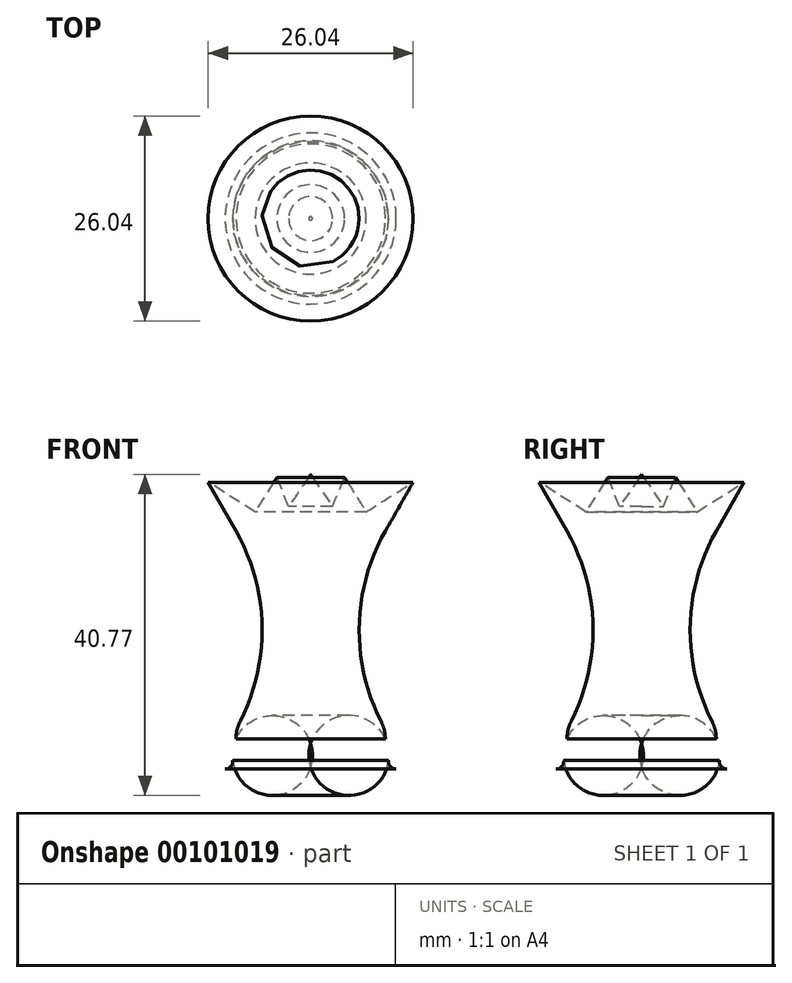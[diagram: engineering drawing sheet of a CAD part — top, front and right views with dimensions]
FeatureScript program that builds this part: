
annotation { "Feature Type Name" : "Feature", "Feature Type Description" : "" }
export const myFeature = defineFeature(function(context is Context, id is Id, definition is map)
    precondition{}
    {
        {
            var Q0;
            Q0=qCreatedBy(makeId("Front.planeOp"),FACE);
            var sketch = newSketch(context, id + "F0", { "sketchPlane" : qUnion([Q0])});
            skLineSegment(sketch, "E0", {"start": v(0, -30.22) * mm, "end": v(10.87, -30.22) * mm});
            skArc(sketch, "E1", {"start": v(10.87, -28.26) * mm, "mid": v(9.89, -29.24) * mm, "end": v(10.87, -30.22) * mm});
            skLineSegment(sketch, "E2", {"start": v(10.87, -28.26) * mm, "end": v(9.49, -26.41) * mm});
            skLineSegment(sketch, "E3", {"start": v(9.49, -26.41) * mm, "end": v(9.49, -25.14) * mm});
            skArc(sketch, "E4", {"start": v(9.49, 0) * mm, "mid": v(6.16, -12.57) * mm, "end": v(9.49, -25.14) * mm});
            skLineSegment(sketch, "E5", {"start": v(9.49, 0) * mm, "end": v(13.02, 6.2) * mm});
            skLineSegment(sketch, "E6", {"start": v(13.02, 6.2) * mm, "end": v(7.06, 2.45) * mm});
            skLineSegment(sketch, "E7", {"start": v(7.06, 2.45) * mm, "end": v(4.3, 6.83) * mm});
            skLineSegment(sketch, "E8", {"start": v(4.3, 6.83) * mm, "end": v(2.79, 3.15) * mm});
            skLineSegment(sketch, "E9", {"start": v(2.79, 3.15) * mm, "end": v(0, 7.19) * mm});
            skLineSegment(sketch, "E10", {"start": v(0, 7.19) * mm, "end": v(0, -30.22) * mm});
            skSolve(sketch);
        }
        {
            var Q0;
            Q0 = qSketchRegion(id + "F0", true);
            var Q1;
            Q1=sQuery(id+"F0.wireOp",EDGE,"E10");
            revolve(context, id + "F1", {"entities" : qUnion([Q0]), "axis" : qUnion([Q1]), "revolveType" : RevolveType.FULL});
        }
        {
            var Q0;
            Q0=makeQuery(id+"F1.opRevolve","SWEPT_EDGE",EDGE,{"disambiguationData":[OSD([sQuery(id+"F0.wireOp",EDGE,"E1"),sQuery(id+"F0.wireOp",EDGE,"E2")])]});
            var Q1;
            Q1=makeQuery(id+"F1.opRevolve","SWEPT_EDGE",EDGE,{"disambiguationData":[OSD([sQuery(id+"F0.wireOp",EDGE,"E3"),sQuery(id+"F0.wireOp",EDGE,"E4")])]});
            var Q2;
            Q2=makeQuery(id+"F1.opRevolve","SWEPT_EDGE",EDGE,{"disambiguationData":[OSD([sQuery(id+"F0.wireOp",EDGE,"E4"),sQuery(id+"F0.wireOp",EDGE,"E5")])]});
            fillet(context, id + "F2", {"entities" : qUnion([Q0, Q1, Q2]), "radius" : 5.08 * mm, "tangentPropagation" : true, "allowEdgeOverflow" : false});
        }
    });
